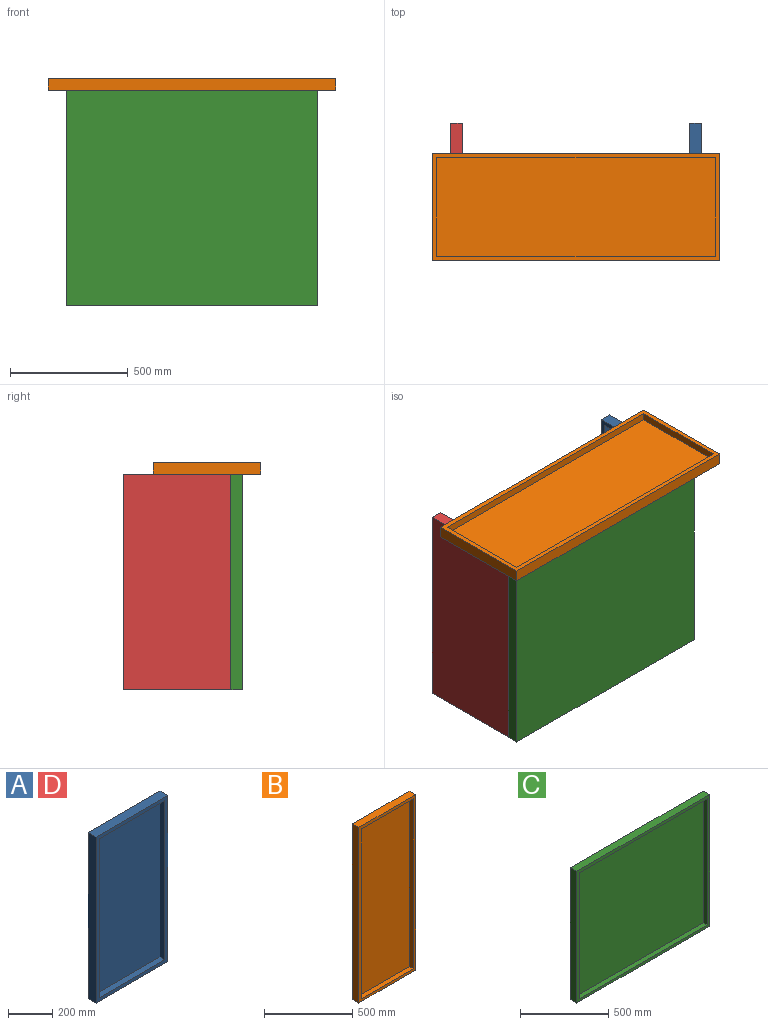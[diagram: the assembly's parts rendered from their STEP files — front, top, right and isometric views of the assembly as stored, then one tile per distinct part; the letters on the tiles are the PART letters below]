
ASSEMBLY  parts=4 mates=3
PART A: 11 faces, bbox 457.2x50.8x914.4 mm
  f0: plane 914.4x50.8mm, normal (-1,0,0), area 46451.5mm2, adj f1,f3,f4,f5
  f1: plane 457.2x50.8mm, normal (0,0,-1), area 23225.8mm2, adj f0,f2,f4,f5
  f2: plane 914.4x50.8mm, normal (1,0,0), area 46451.5mm2, adj f1,f3,f4,f5
  f3: plane 457.2x50.8mm, normal (0,0,1), area 23225.8mm2, adj f0,f2,f4,f5
  f4: plane 914.4x457.2mm, normal (0,-1,0), area 50806.3mm2, adj f0,f1,f2,f3,f6,f7,f8,f9
  f5: plane 914.4x457.2mm, normal (0,1,0), area 418063.7mm2, adj f0,f1,f2,f3
  f6: plane 876.3x31.75mm, normal (1,0,0), area 27822.5mm2, adj f4,f7,f9,f10
  f7: plane 419.1x31.75mm, normal (0,0,1), area 13306.4mm2, adj f4,f6,f8,f10
  f8: plane 876.3x31.75mm, normal (-1,0,0), area 27822.5mm2, adj f4,f7,f9,f10
  f9: plane 419.1x31.75mm, normal (0,0,-1), area 13306.4mm2, adj f4,f6,f8,f10
  f10: plane 876.3x419.1mm, normal (0,-1,0), area 367257.3mm2, adj f6,f7,f8,f9
PART B: 11 faces, bbox 457.2x50.8x1219.2 mm
  f0: plane 1219.2x50.8mm, normal (-1,0,0), area 61935.4mm2, adj f1,f3,f4,f5
  f1: plane 457.2x50.8mm, normal (0,0,-1), area 23225.8mm2, adj f0,f2,f4,f5
  f2: plane 1219.2x50.8mm, normal (1,0,0), area 61935.4mm2, adj f1,f3,f4,f5
  f3: plane 457.2x50.8mm, normal (0,0,1), area 23225.8mm2, adj f0,f2,f4,f5
  f4: plane 1219.2x457.2mm, normal (0,-1,0), area 62419.2mm2, adj f0,f1,f2,f3,f6,f7,f8,f9
  f5: plane 1219.2x457.2mm, normal (0,1,0), area 557418.2mm2, adj f0,f1,f2,f3
  f6: plane 1181.1x31.75mm, normal (1,0,0), area 37499.9mm2, adj f4,f7,f9,f10
  f7: plane 419.1x31.75mm, normal (0,0,1), area 13306.4mm2, adj f4,f6,f8,f10
  f8: plane 1181.1x31.75mm, normal (-1,0,0), area 37499.9mm2, adj f4,f7,f9,f10
  f9: plane 419.1x31.75mm, normal (0,0,-1), area 13306.4mm2, adj f4,f6,f8,f10
  f10: plane 1181.1x419.1mm, normal (0,-1,0), area 494999mm2, adj f6,f7,f8,f9
PART C: 11 faces, bbox 1066.8x50.8x914.4 mm
  f0: plane 914.4x50.8mm, normal (1,0,0), area 46451.5mm2, adj f1,f3,f4,f5
  f1: plane 1066.8x50.8mm, normal (0,0,1), area 54193.4mm2, adj f0,f2,f4,f5
  f2: plane 914.4x50.8mm, normal (-1,0,0), area 46451.5mm2, adj f1,f3,f4,f5
  f3: plane 1066.8x50.8mm, normal (0,0,-1), area 54193.4mm2, adj f0,f2,f4,f5
  f4: plane 1066.8x914.4mm, normal (0,-1,0), area 74032.1mm2, adj f0,f1,f2,f3,f6,f7,f8,f9
  f5: plane 1066.8x914.4mm, normal (0,1,0), area 975481.9mm2, adj f0,f1,f2,f3
  f6: plane 876.3x31.75mm, normal (-1,0,0), area 27822.5mm2, adj f4,f7,f9,f10
  f7: plane 1028.7x31.75mm, normal (0,0,-1), area 32661.2mm2, adj f4,f6,f8,f10
  f8: plane 876.3x31.75mm, normal (1,0,0), area 27822.5mm2, adj f4,f7,f9,f10
  f9: plane 1028.7x31.75mm, normal (0,0,1), area 32661.2mm2, adj f4,f6,f8,f10
  f10: plane 1028.7x876.3mm, normal (0,-1,0), area 901449.8mm2, adj f6,f7,f8,f9
PART D: same geometry as A
PLACE A rot(axis=(0,0,-1),90deg) t=(1250.71,-1710.61,-796.72)mm
PLACE B rot(axis=(-0.58,-0.58,0.58),120deg) t=(6133.74,-6651.13,424.78)mm
PLACE C rot(axis=(0,0,-1),180deg) t=(6419.79,200.9,-2160.14)mm fixed
PLACE D rot(axis=(0,0,1),90deg) t=(183.91,3318.9,-796.72)mm
MATE fastened B.f5 <-> C.f1  axis (0,0,-1) through (107.71,448.55,678.78)mm
MATE fastened D.f5 <-> C.f0  axis (-1,0,0) through (183.91,575.55,-235.62)mm
MATE fastened A.f5 <-> C.f2  axis (1,0,0) through (1250.71,575.55,-235.62)mm
